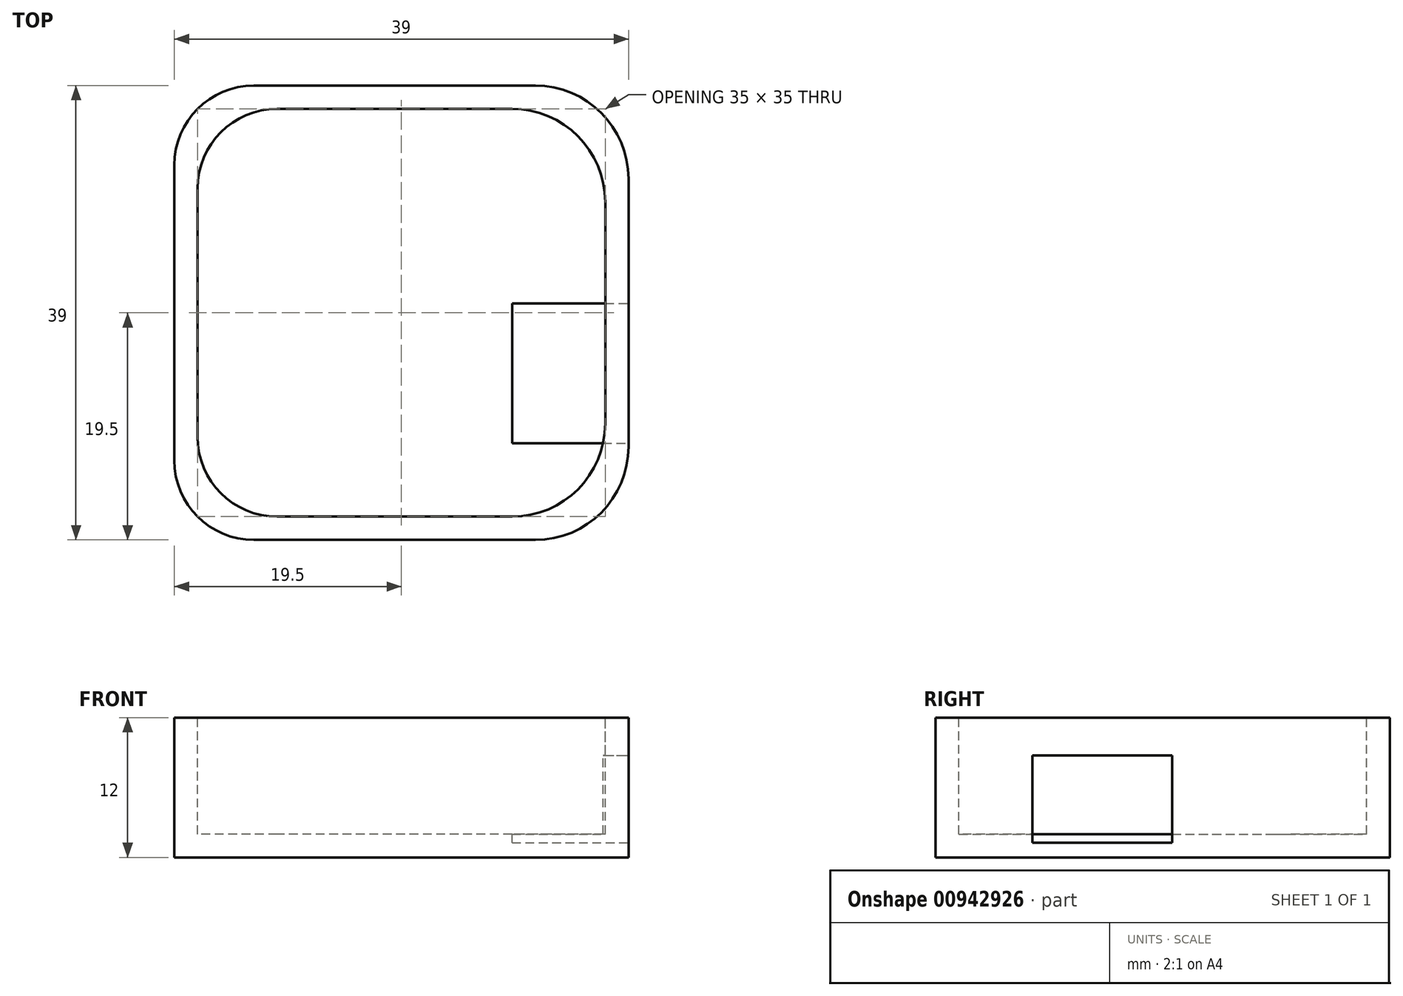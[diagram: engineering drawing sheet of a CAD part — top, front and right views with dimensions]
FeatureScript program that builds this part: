
annotation { "Feature Type Name" : "Feature", "Feature Type Description" : "" }
export const myFeature = defineFeature(function(context is Context, id is Id, definition is map)
    precondition{}
    {
        {
            var Q0;
            Q0=qCreatedBy(makeId("Top.planeOp"),FACE);
            var sketch = newSketch(context, id + "F0", { "sketchPlane" : qUnion([Q0])});
            skLineSegment(sketch, "E0.bottom", {"start": v(11.5, -19.5) * mm, "end": v(-12.67, -19.5) * mm});
            skLineSegment(sketch, "E0.top", {"start": v(11.5, 19.5) * mm, "end": v(-12.67, 19.5) * mm});
            skLineSegment(sketch, "E0.left", {"start": v(19.5, -11.5) * mm, "end": v(19.5, 11.5) * mm});
            skLineSegment(sketch, "E0.right", {"start": v(-19.5, -12.67) * mm, "end": v(-19.5, 12.67) * mm});
            skPoint(sketch, "E0.middle", {"position": v(0, 0) * mm});
            skPoint(sketch, "E1.visualSharp", {"position": v(-19.5, 19.5) * mm});
            skArc(sketch, "E1.filletArc", {"start": v(-12.67, 19.5) * mm, "mid": v(-17.5, 17.5) * mm, "end": v(-19.5, 12.67) * mm});
            skPoint(sketch, "E2.visualSharp", {"position": v(-19.5, -19.5) * mm});
            skArc(sketch, "E2.filletArc", {"start": v(-19.5, -12.67) * mm, "mid": v(-17.5, -17.5) * mm, "end": v(-12.67, -19.5) * mm});
            skPoint(sketch, "E3.visualSharp", {"position": v(19.5, 19.5) * mm});
            skArc(sketch, "E3.filletArc", {"start": v(19.5, 11.5) * mm, "mid": v(17.16, 17.16) * mm, "end": v(11.5, 19.5) * mm});
            skPoint(sketch, "E4.visualSharp", {"position": v(19.5, -19.5) * mm});
            skArc(sketch, "E4.filletArc", {"start": v(11.5, -19.5) * mm, "mid": v(17.16, -17.16) * mm, "end": v(19.5, -11.5) * mm});
            skSolve(sketch);
        }
        {
            var Q0;
            Q0=makeQuery(id+"F0.imprint","IMPRINT",FACE,{"disambiguationData":[TD([[makeQuery(id+"F0.imprint","IMPRINT",EDGE,{"derivedFrom":sQuery(id+"F0.wireOp",EDGE,"E0.bottom")}),-1.0]])]});
            extrude(context, id + "F1", {"entities" : qUnion([Q0]), "depth" : 12 * mm, "offsetDistance" : 25 * mm});
        }
        {
            var Q0;
            Q0=makeQuery(id+"F1.opExtrude","CAP_FACE",FACE,{"disambiguationData":[OSD([sQuery(id+"F0.wireOp",EDGE,"E0.bottom"),sQuery(id+"F0.wireOp",EDGE,"E0.top"),sQuery(id+"F0.wireOp",EDGE,"E0.left"),sQuery(id+"F0.wireOp",EDGE,"E0.right"),sQuery(id+"F0.wireOp",EDGE,"E1.filletArc"),sQuery(id+"F0.wireOp",EDGE,"E2.filletArc"),sQuery(id+"F0.wireOp",EDGE,"E3.filletArc"),sQuery(id+"F0.wireOp",EDGE,"E4.filletArc")])],"isStart":false});
            var sketch = newSketch(context, id + "F2", { "sketchPlane" : qUnion([Q0])});
            skLineSegment(sketch, "E5.bottom", {"start": v(9.5, -17.5) * mm, "end": v(-10.67, -17.5) * mm});
            skLineSegment(sketch, "E5.top", {"start": v(9.5, 17.5) * mm, "end": v(-10.67, 17.5) * mm});
            skLineSegment(sketch, "E5.left", {"start": v(17.5, -9.5) * mm, "end": v(17.5, 9.5) * mm});
            skLineSegment(sketch, "E5.right", {"start": v(-17.5, -10.67) * mm, "end": v(-17.5, 10.67) * mm});
            skPoint(sketch, "E5.middle", {"position": v(0, 0) * mm});
            skPoint(sketch, "E6.visualSharp", {"position": v(-17.5, 17.5) * mm});
            skArc(sketch, "E6.filletArc", {"start": v(-10.67, 17.5) * mm, "mid": v(-15.5, 15.5) * mm, "end": v(-17.5, 10.67) * mm});
            skPoint(sketch, "E7.visualSharp", {"position": v(-17.5, -17.5) * mm});
            skArc(sketch, "E7.filletArc", {"start": v(-17.5, -10.67) * mm, "mid": v(-15.5, -15.5) * mm, "end": v(-10.67, -17.5) * mm});
            skPoint(sketch, "E8.visualSharp", {"position": v(17.5, 17.5) * mm});
            skArc(sketch, "E8.filletArc", {"start": v(17.5, 9.5) * mm, "mid": v(15.16, 15.16) * mm, "end": v(9.5, 17.5) * mm});
            skPoint(sketch, "E9.visualSharp", {"position": v(17.5, -17.5) * mm});
            skArc(sketch, "E9.filletArc", {"start": v(9.5, -17.5) * mm, "mid": v(15.16, -15.16) * mm, "end": v(17.5, -9.5) * mm});
            skSolve(sketch);
        }
        {
            var Q0;
            Q0=makeQuery(id+"F2.imprint","IMPRINT",FACE,{"disambiguationData":[TD([[makeQuery(id+"F2.imprint","IMPRINT",EDGE,{"derivedFrom":sQuery(id+"F2.wireOp",EDGE,"E5.bottom")}),-1.0]])]});
            extrude(context, id + "F3", {"entities" : qUnion([Q0]), "operationType" : NewBodyOperationType.REMOVE, "oppositeDirection" : true, "depth" : 10 * mm, "offsetDistance" : 25 * mm});
        }
        {
            var Q0;
            Q0=makeQuery(id+"F1.opExtrude","SWEPT_FACE",FACE,{"disambiguationData":[OSD([sQuery(id+"F0.wireOp",EDGE,"E0.left")])]});
            var sketch = newSketch(context, id + "F4", { "sketchPlane" : qUnion([Q0])});
            skLineSegment(sketch, "E10.bottom", {"start": v(-11.2, 1.25) * mm, "end": v(0.8, 1.25) * mm});
            skLineSegment(sketch, "E10.top", {"start": v(-11.2, 8.75) * mm, "end": v(0.8, 8.75) * mm});
            skLineSegment(sketch, "E10.left", {"start": v(-11.2, 1.25) * mm, "end": v(-11.2, 8.75) * mm});
            skLineSegment(sketch, "E10.right", {"start": v(0.8, 1.25) * mm, "end": v(0.8, 8.75) * mm});
            skPoint(sketch, "E10.middle", {"position": v(-5.2, 5) * mm});
            skSolve(sketch);
        }
        {
            var Q0;
            Q0=makeQuery(id+"F4.imprint","IMPRINT",FACE,{"disambiguationData":[TD([[makeQuery(id+"F4.imprint","IMPRINT",EDGE,{"derivedFrom":sQuery(id+"F4.wireOp",EDGE,"E10.bottom")}),1.0]])]});
            extrude(context, id + "F5", {"entities" : qUnion([Q0]), "operationType" : NewBodyOperationType.REMOVE, "oppositeDirection" : true, "depth" : 10 * mm, "offsetDistance" : 25 * mm});
        }
    });
